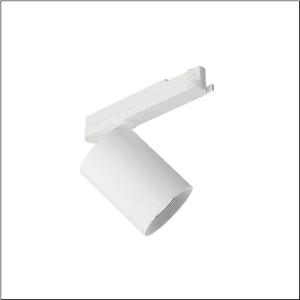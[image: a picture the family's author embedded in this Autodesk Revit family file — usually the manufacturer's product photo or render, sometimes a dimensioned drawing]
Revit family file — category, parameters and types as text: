
# Revit family: spot_21_51se12mbb5b
name_source: partatom
category: Lighting Fixtures
units: mm (PartAtom-declared; Revit-internal decimal feet)

## family parameters
Cut with Voids When Loaded = No
Host = Face
Light Source = No
Part Type = Normal
Room Calculation Point = No
Round Connector Dimension = Use Diameter
Shared = No

## types (1)
- --- (1 x LED, 5300 lm, 41.7 W, 3000K)
    Apparent Load = 42 VA
    CIE Flux Codes = 95 98 99 100 100
    Color Rendering = 90
    Color Temperature = 3000K
    Default Elevation = 1800 mm
    Description = Spot 21, directional spotlight, light control with lens, of PMMA, LED rated luminous flux: 5.100lm, light colour: 930, control gear: ECG Multilumen, with 3-phase adapter, mains connection: 220..240V, AC, 50/60Hz, of aluminium, traffic white (RAL 9016), length: 213mm, diameter: 105mm, protection rating (complete): IP20, insulation class (complete): insulation class I (protective earthing), certification: CE, impact resistance: IK02, permissible ambient temperature for indoor applications: -20..+40°C, packaging unit: 1 piece
    Height = 175 mm
    Lamp = 1 x LED
    Lamp Light Flux = 5300 lm
    Lamp Power = 41.7 W
    Lamp count = 1
    Length = 105 mm
    Luminous efficacy = 127 lm/W
    Manufacturer = Siteco
    ModVariant = No
    Model = 51SE12MBB5B
    Mounting Place = Ceiling
    Mounting Type = Pendant
    Number of Poles = 1
    OnlyDefault = Yes
    Power Factor = 1
    Product Name = Spot 21
    Product group = directional spotlight
    ProductGroupID = 905
    Protection Class = Protection class I
    Protection Degree = IP 20
    RLX_Detail_Level = 1
    RLX_Emergency_Light_Flux = 0 lm
    RLX_Emergency_Type = 0
    RLX_Emergency_Type_DB = No
    RlxData = <blob elided: 17633 chars, md5=5953312e>
    Socket = socket
    Standby Power = 0 W
    System Light Flux = 5300 lm
    System Power = 42 W
    Type Comments = factory setting: luminous flux: 100 % | (ON | ON | ON | ON) | 1050 mA
    Type Image = l_1003976.jpg
    URL = http://relux.com
    VarID = @adj_075861
    Voltage = 0 V
    Weight = 0.00 kg
    Width = 0 mm  [stored 0 ft]

note: [stored X ft] marks values corroborated as IEEE doubles in the binary element streams (Revit-internal decimal feet)

## geometry (parser evidence)
native form markers: Blend x4, Sweep x12
no freeform markers — native parametric forms only
